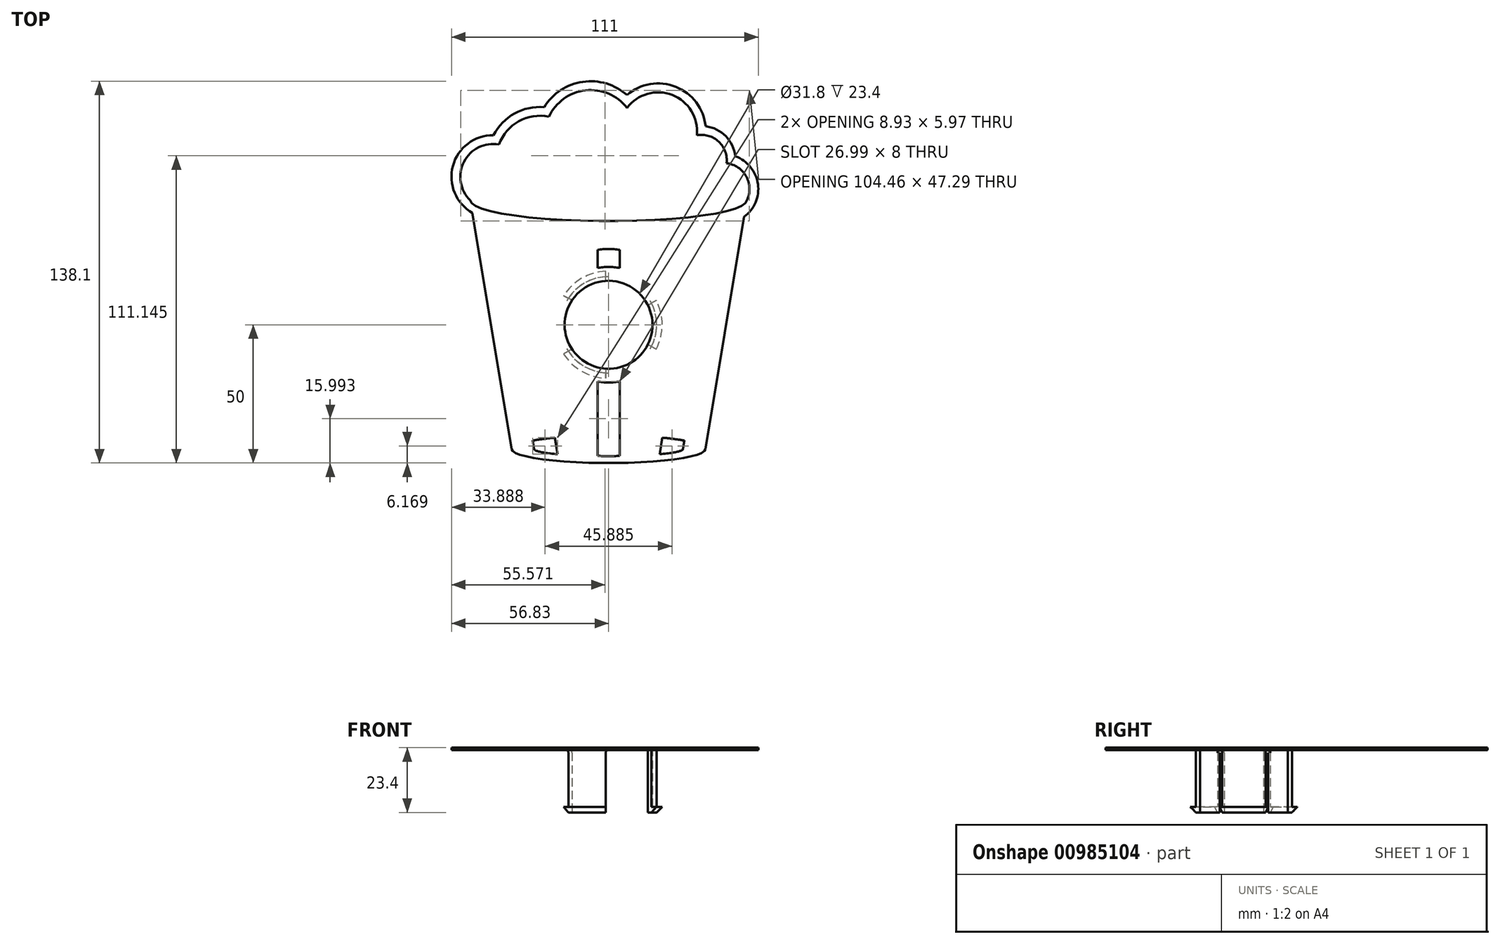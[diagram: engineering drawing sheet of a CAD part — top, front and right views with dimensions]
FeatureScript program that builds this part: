
annotation { "Feature Type Name" : "Feature", "Feature Type Description" : "" }
export const myFeature = defineFeature(function(context is Context, id is Id, definition is map)
    precondition{}
    {
        {
            var Q0;
            Q0=qCreatedBy(makeId("Top.planeOp"),FACE);
            var sketch = newSketch(context, id + "F0", { "sketchPlane" : qUnion([Q0])});
            skCircle(sketch, "E0", {"center": v(0, 0) * mm, "radius": 17.4 * mm});
            skCircle(sketch, "E1", {"center": v(0, 0) * mm, "radius": 15.9 * mm});
            skCircle(sketch, "E2", {"center": v(0, 0) * mm, "radius": 27.4 * mm});
            skLineSegment(sketch, "E3", {"start": v(0, 0) * mm, "end": v(0, 17.75) * mm, "construction": true});
            skText(sketch, "E4", { "text": "o", "fontName": "RobotoSlab-Bold.ttf"});
            skText(sketch, "E5", { "text": "u", "fontName": "RobotoSlab-Bold.ttf"});
            skText(sketch, "E6", { "text": "e", "fontName": "RobotoSlab-Bold.ttf"});
            skText(sketch, "E7", { "text": "i", "fontName": "RobotoSlab-Bold.ttf"});
            skText(sketch, "E8", { "text": "r", "fontName": "RobotoSlab-Bold.ttf"});
            skText(sketch, "E9", { "text": "c", "fontName": "RobotoSlab-Bold.ttf"});
            skText(sketch, "E10", { "text": "e", "fontName": "RobotoSlab-Bold.ttf"});
            skText(sketch, "E11", { "text": "o", "fontName": "RobotoSlab-Bold.ttf"});
            skText(sketch, "E12", { "text": "r", "fontName": "RobotoSlab-Bold.ttf"});
            skText(sketch, "E13", { "text": "n", "fontName": "RobotoSlab-Bold.ttf"});
            skLineSegment(sketch, "E14.2.0", {"start": v(0, 0) * mm, "end": v(-15.37, 8.88) * mm, "construction": true});
            skLineSegment(sketch, "E14.3.0", {"start": v(0, 0) * mm, "end": v(-17.75, 0) * mm, "construction": true});
            skLineSegment(sketch, "E14.4.0", {"start": v(0, 0) * mm, "end": v(-15.37, -8.88) * mm, "construction": true});
            skLineSegment(sketch, "E14.5.0", {"start": v(0, 0) * mm, "end": v(-8.88, -15.37) * mm, "construction": true});
            skLineSegment(sketch, "E14.6.0", {"start": v(0, 0) * mm, "end": v(0, -17.75) * mm, "construction": true});
            skLineSegment(sketch, "E14.7.0", {"start": v(0, 0) * mm, "end": v(8.87, -15.37) * mm, "construction": true});
            skLineSegment(sketch, "E14.8.0", {"start": v(0, 0) * mm, "end": v(15.37, -8.88) * mm, "construction": true});
            skLineSegment(sketch, "E14.9.0", {"start": v(0, 0) * mm, "end": v(17.75, 0) * mm, "construction": true});
            skLineSegment(sketch, "E14.10.0", {"start": v(0, 0) * mm, "end": v(15.37, 8.87) * mm, "construction": true});
            skLineSegment(sketch, "E14.11.0", {"start": v(0, 0) * mm, "end": v(8.88, 15.37) * mm, "construction": true});
            skText(sketch, "E15", { "text": "S", "fontName": "RobotoSlab-Bold.ttf"});
            skLineSegment(sketch, "E16", {"start": v(0, 0) * mm, "end": v(-8.88, 15.37) * mm, "construction": true});
            const initialGuessF0  = {"E4": [-0.00328, 0.01775, 1, 0, 0.008], "E5": [0.0057, 0.0172, 0.86603, -0.5, 0.008], "E6": [0.01692, -0.0062, -0.5, -0.86603, 0.008], "E7": [-0.0071, -0.0164, -0.86603, 0.5, 0.008], "E8": [-0.01407, -0.01114, -0.5, 0.86603, 0.008], "E9": [0.01775, 0.0031, 0, -1, 0.008], "E10": [0.01156, -0.01382, -0.86603, -0.5, 0.008], "E11": [-0.01775, -0.00328, 0, 1, 0.008], "E12": [0.01407, 0.01114, 0.5, -0.86603, 0.008], "E13": [-0.01726, 0.0056, 0.5, 0.86603, 0.008], "E15": [-0.01195, 0.0136, 0.86603, 0.5, 0.008]};
            skSetInitialGuess(sketch, initialGuessF0);
            skSolve(sketch);
        }
        {
            var Q0;
            Q0=makeQuery(id+"F0.imprint","IMPRINT",FACE,{"disambiguationData":[TD([[makeQuery(id+"F0.imprint","IMPRINT",EDGE,{"derivedFrom":sQuery(id+"F0.wireOp",EDGE,"E0")}),1.0]])]});
            var Q1;
            Q1=makeQuery(id+"F0.imprint","IMPRINT",FACE,{"disambiguationData":[TD([[makeQuery(id+"F0.imprint","IMPRINT",EDGE,{"derivedFrom":sQuery(id+"F0.wireOp",EDGE,"E4.sketch_text.stroke-0")}),-1.0]])]});
            var Q2;
            Q2=makeQuery(id+"F0.imprint","IMPRINT",FACE,{"disambiguationData":[TD([[makeQuery(id+"F0.imprint","IMPRINT",EDGE,{"derivedFrom":sQuery(id+"F0.wireOp",EDGE,"E7.sketch_text.stroke-0")}),-1.0]])]});
            var Q3;
            Q3=makeQuery(id+"F0.imprint","IMPRINT",FACE,{"disambiguationData":[TD([[makeQuery(id+"F0.imprint","IMPRINT",EDGE,{"derivedFrom":sQuery(id+"F0.wireOp",EDGE,"E11.sketch_text.stroke-10")}),1.0]])]});
            var Q4;
            Q4=makeQuery(id+"F0.imprint","IMPRINT",FACE,{"disambiguationData":[TD([[makeQuery(id+"F0.imprint","IMPRINT",EDGE,{"derivedFrom":sQuery(id+"F0.wireOp",EDGE,"E9.sketch_text.stroke-0")}),-1.0]])]});
            var Q5;
            Q5=makeQuery(id+"F0.imprint","IMPRINT",FACE,{"disambiguationData":[TD([[makeQuery(id+"F0.imprint","IMPRINT",EDGE,{"derivedFrom":sQuery(id+"F0.wireOp",EDGE,"E10.sketch_text.stroke-0")}),-1.0]])]});
            var Q6;
            Q6=makeQuery(id+"F0.imprint","IMPRINT",FACE,{"disambiguationData":[TD([[makeQuery(id+"F0.imprint","IMPRINT",EDGE,{"derivedFrom":sQuery(id+"F0.wireOp",EDGE,"E6.sketch_text.stroke-0")}),-1.0]])]});
            var Q7;
            Q7=makeQuery(id+"F0.imprint","IMPRINT",FACE,{"disambiguationData":[TD([[makeQuery(id+"F0.imprint","IMPRINT",EDGE,{"derivedFrom":sQuery(id+"F0.wireOp",EDGE,"E12.sketch_text.stroke-0")}),-1.0]])]});
            var Q8;
            Q8=makeQuery(id+"F0.imprint","IMPRINT",FACE,{"disambiguationData":[TD([[makeQuery(id+"F0.imprint","IMPRINT",EDGE,{"derivedFrom":sQuery(id+"F0.wireOp",EDGE,"E5.sketch_text.stroke-0")}),-1.0]])]});
            var Q9;
            Q9=makeQuery(id+"F0.imprint","IMPRINT",FACE,{"disambiguationData":[TD([[makeQuery(id+"F0.imprint","IMPRINT",EDGE,{"derivedFrom":sQuery(id+"F0.wireOp",EDGE,"E0")}),-1.0]])]});
            var Q10;
            Q10=makeQuery(id+"F0.imprint","IMPRINT",FACE,{"disambiguationData":[TD([[makeQuery(id+"F0.imprint","IMPRINT",EDGE,{"derivedFrom":sQuery(id+"F0.wireOp",EDGE,"E5.sketch_text.stroke-10")}),1.0]])]});
            var Q11;
            Q11=makeQuery(id+"F0.imprint","IMPRINT",FACE,{"disambiguationData":[TD([[makeQuery(id+"F0.imprint","IMPRINT",EDGE,{"derivedFrom":sQuery(id+"F0.wireOp",EDGE,"E13.sketch_text.stroke-0")}),-1.0]])]});
            var Q12;
            Q12=makeQuery(id+"F0.imprint","IMPRINT",FACE,{"disambiguationData":[TD([[makeQuery(id+"F0.imprint","IMPRINT",EDGE,{"derivedFrom":sQuery(id+"F0.wireOp",EDGE,"E8.sketch_text.stroke-0")}),-1.0]])]});
            var Q13;
            Q13=makeQuery(id+"F0.imprint","IMPRINT",FACE,{"disambiguationData":[TD([[makeQuery(id+"F0.imprint","IMPRINT",EDGE,{"derivedFrom":sQuery(id+"F0.wireOp",EDGE,"E11.sketch_text.stroke-0")}),-1.0]])]});
            var Q14;
            Q14=makeQuery(id+"F0.imprint","IMPRINT",FACE,{"disambiguationData":[TD([[makeQuery(id+"F0.imprint","IMPRINT",EDGE,{"derivedFrom":sQuery(id+"F0.wireOp",EDGE,"E7.sketch_text.stroke-10")}),-1.0]])]});
            var Q15;
            Q15=makeQuery(id+"F0.imprint","IMPRINT",FACE,{"disambiguationData":[TD([[makeQuery(id+"F0.imprint","IMPRINT",EDGE,{"derivedFrom":sQuery(id+"F0.wireOp",EDGE,"E10.sketch_text.stroke-17")}),1.0]])]});
            var Q16;
            Q16=makeQuery(id+"F0.imprint","IMPRINT",FACE,{"disambiguationData":[TD([[makeQuery(id+"F0.imprint","IMPRINT",EDGE,{"derivedFrom":sQuery(id+"F0.wireOp",EDGE,"E15.sketch_text.stroke-0")}),-1.0]])]});
            var Q17;
            Q17=makeQuery(id+"F0.imprint","IMPRINT",FACE,{"disambiguationData":[TD([[makeQuery(id+"F0.imprint","IMPRINT",EDGE,{"derivedFrom":sQuery(id+"F0.wireOp",EDGE,"E4.sketch_text.stroke-10")}),1.0]])]});
            var Q18;
            Q18=makeQuery(id+"F0.imprint","IMPRINT",FACE,{"disambiguationData":[TD([[makeQuery(id+"F0.imprint","IMPRINT",EDGE,{"derivedFrom":sQuery(id+"F0.wireOp",EDGE,"E6.sketch_text.stroke-17")}),1.0]])]});
            extrude(context, id + "F1", {"entities" : qUnion([Q0, Q1, Q2, Q3, Q4, Q5, Q6, Q7, Q8, Q9, Q10, Q11, Q12, Q13, Q14, Q15, Q16, Q17, Q18]), "depth" : 0.8 * mm, "offsetDistance" : 25 * mm});
        }
        {
            var Q0;
            Q0=makeQuery(id+"F0.imprint","IMPRINT",FACE,{"disambiguationData":[TD([[makeQuery(id+"F0.imprint","IMPRINT",EDGE,{"derivedFrom":sQuery(id+"F0.wireOp",EDGE,"E0")}),1.0]])]});
            extrude(context, id + "F2", {"entities" : qUnion([Q0]), "operationType" : NewBodyOperationType.ADD, "oppositeDirection" : true, "depth" : 22.6 * mm, "offsetDistance" : 25 * mm});
        }
        {
            var Q0;
            Q0=makeQuery(id+"F2.opExtrude","CAP_FACE",FACE,{"disambiguationData":[OSD([sQuery(id+"F0.wireOp",EDGE,"E0"),sQuery(id+"F0.wireOp",EDGE,"E1")])],"isStart":false});
            var sketch = newSketch(context, id + "F3", { "sketchPlane" : qUnion([Q0])});
            skLineSegment(sketch, "E17.bottom", {"start": v(1, 0) * mm, "end": v(-1, 0) * mm});
            skLineSegment(sketch, "E17.top", {"start": v(1, -20) * mm, "end": v(-1, -20) * mm});
            skLineSegment(sketch, "E17.left", {"start": v(1, 0) * mm, "end": v(1, -20) * mm});
            skLineSegment(sketch, "E17.right", {"start": v(-1, 0) * mm, "end": v(-1, -20) * mm});
            skLineSegment(sketch, "E18.1.0", {"start": v(0.5, 0.87) * mm, "end": v(-0.5, -0.87) * mm});
            skLineSegment(sketch, "E18.1.1", {"start": v(17.82, -9.13) * mm, "end": v(16.82, -10.87) * mm});
            skLineSegment(sketch, "E18.1.2", {"start": v(-0.5, -0.87) * mm, "end": v(16.82, -10.87) * mm});
            skLineSegment(sketch, "E18.1.3", {"start": v(0.5, 0.87) * mm, "end": v(17.82, -9.13) * mm});
            skLineSegment(sketch, "E18.2.0", {"start": v(-0.5, 0.87) * mm, "end": v(0.5, -0.87) * mm});
            skLineSegment(sketch, "E18.2.1", {"start": v(16.82, 10.87) * mm, "end": v(17.82, 9.13) * mm});
            skLineSegment(sketch, "E18.2.2", {"start": v(0.5, -0.87) * mm, "end": v(17.82, 9.13) * mm});
            skLineSegment(sketch, "E18.2.3", {"start": v(-0.5, 0.87) * mm, "end": v(16.82, 10.87) * mm});
            skLineSegment(sketch, "E18.3.0", {"start": v(-1, 0) * mm, "end": v(1, 0) * mm});
            skLineSegment(sketch, "E18.3.1", {"start": v(-1, 20) * mm, "end": v(1, 20) * mm});
            skLineSegment(sketch, "E18.3.2", {"start": v(1, 0) * mm, "end": v(1, 20) * mm});
            skLineSegment(sketch, "E18.3.3", {"start": v(-1, 0) * mm, "end": v(-1, 20) * mm});
            skLineSegment(sketch, "E18.4.0", {"start": v(-0.5, -0.87) * mm, "end": v(0.5, 0.87) * mm});
            skLineSegment(sketch, "E18.4.1", {"start": v(-17.82, 9.13) * mm, "end": v(-16.82, 10.87) * mm});
            skLineSegment(sketch, "E18.4.2", {"start": v(0.5, 0.87) * mm, "end": v(-16.82, 10.87) * mm});
            skLineSegment(sketch, "E18.4.3", {"start": v(-0.5, -0.87) * mm, "end": v(-17.82, 9.13) * mm});
            skLineSegment(sketch, "E18.5.0", {"start": v(0.5, -0.87) * mm, "end": v(-0.5, 0.87) * mm});
            skLineSegment(sketch, "E18.5.1", {"start": v(-16.82, -10.87) * mm, "end": v(-17.82, -9.13) * mm});
            skLineSegment(sketch, "E18.5.2", {"start": v(-0.5, 0.87) * mm, "end": v(-17.82, -9.13) * mm});
            skLineSegment(sketch, "E18.5.3", {"start": v(0.5, -0.87) * mm, "end": v(-16.82, -10.87) * mm});
            skPoint(sketch, "E18.center", {"position": v(0, 0) * mm});
            skCircle(sketch, "E19", {"center": v(0, 0) * mm, "radius": 19.4 * mm});
            skSolve(sketch);
        }
        {
            var Q0;
            {var subQ0=sQuery(id+"F3.wireOp",EDGE,"E18.1.2");var subQ1=makeQuery(id+"F2.opExtrude","CAP_EDGE",EDGE,{"disambiguationData":[OSD([sQuery(id+"F0.wireOp",EDGE,"E1")])],"isStart":false});var subQ2=makeQuery(id+"F3.imprint","INTERSECT",VERTEX,{"derivedFrom":[subQ1,subQ0]});Q0=makeQuery(id+"F3.imprint","IMPRINT",FACE,{"disambiguationData":[TD([[makeQuery(id+"F3.imprint","IMPRINT",EDGE,{"disambiguationData":[TD([[subQ2,-1.0]])],"derivedFrom":subQ0}),1.0]])]});}
            var Q1;
            {var subQ0=sQuery(id+"F3.wireOp",EDGE,"E17.left");var subQ1=makeQuery(id+"F2.opExtrude","CAP_EDGE",EDGE,{"disambiguationData":[OSD([sQuery(id+"F0.wireOp",EDGE,"E1")])],"isStart":false});var subQ2=makeQuery(id+"F3.imprint","INTERSECT",VERTEX,{"derivedFrom":[subQ1,subQ0]});Q1=makeQuery(id+"F3.imprint","IMPRINT",FACE,{"disambiguationData":[TD([[makeQuery(id+"F3.imprint","IMPRINT",EDGE,{"disambiguationData":[TD([[subQ2,-1.0]])],"derivedFrom":subQ0}),-1.0]])]});}
            var Q2;
            {var subQ0=sQuery(id+"F3.wireOp",EDGE,"E18.5.2");var subQ1=makeQuery(id+"F2.opExtrude","CAP_EDGE",EDGE,{"disambiguationData":[OSD([sQuery(id+"F0.wireOp",EDGE,"E1")])],"isStart":false});var subQ2=makeQuery(id+"F3.imprint","INTERSECT",VERTEX,{"derivedFrom":[subQ1,subQ0]});Q2=makeQuery(id+"F3.imprint","IMPRINT",FACE,{"disambiguationData":[TD([[makeQuery(id+"F3.imprint","IMPRINT",EDGE,{"disambiguationData":[TD([[subQ2,-1.0]])],"derivedFrom":subQ0}),1.0]])]});}
            var Q3;
            {var subQ0=sQuery(id+"F3.wireOp",EDGE,"E18.4.2");var subQ1=makeQuery(id+"F2.opExtrude","CAP_EDGE",EDGE,{"disambiguationData":[OSD([sQuery(id+"F0.wireOp",EDGE,"E1")])],"isStart":false});var subQ2=makeQuery(id+"F3.imprint","INTERSECT",VERTEX,{"derivedFrom":[subQ1,subQ0]});Q3=makeQuery(id+"F3.imprint","IMPRINT",FACE,{"disambiguationData":[TD([[makeQuery(id+"F3.imprint","IMPRINT",EDGE,{"disambiguationData":[TD([[subQ2,-1.0]])],"derivedFrom":subQ0}),1.0]])]});}
            var Q4;
            {var subQ0=sQuery(id+"F3.wireOp",EDGE,"E18.3.2");var subQ1=makeQuery(id+"F2.opExtrude","CAP_EDGE",EDGE,{"disambiguationData":[OSD([sQuery(id+"F0.wireOp",EDGE,"E1")])],"isStart":false});var subQ2=makeQuery(id+"F3.imprint","INTERSECT",VERTEX,{"derivedFrom":[subQ1,subQ0]});Q4=makeQuery(id+"F3.imprint","IMPRINT",FACE,{"disambiguationData":[TD([[makeQuery(id+"F3.imprint","IMPRINT",EDGE,{"disambiguationData":[TD([[subQ2,-1.0]])],"derivedFrom":subQ0}),1.0]])]});}
            var Q5;
            {var subQ0=sQuery(id+"F3.wireOp",EDGE,"E18.2.2");var subQ1=makeQuery(id+"F2.opExtrude","CAP_EDGE",EDGE,{"disambiguationData":[OSD([sQuery(id+"F0.wireOp",EDGE,"E1")])],"isStart":false});var subQ2=makeQuery(id+"F3.imprint","INTERSECT",VERTEX,{"derivedFrom":[subQ1,subQ0]});Q5=makeQuery(id+"F3.imprint","IMPRINT",FACE,{"disambiguationData":[TD([[makeQuery(id+"F3.imprint","IMPRINT",EDGE,{"disambiguationData":[TD([[subQ2,-1.0]])],"derivedFrom":subQ0}),1.0]])]});}
            var Q6;
            {var subQ0=sQuery(id+"F3.wireOp",EDGE,"E17.left");var subQ1=makeQuery(id+"F2.opExtrude","CAP_EDGE",EDGE,{"disambiguationData":[OSD([sQuery(id+"F0.wireOp",EDGE,"E1")])],"isStart":false});var subQ2=makeQuery(id+"F3.imprint","INTERSECT",VERTEX,{"derivedFrom":[subQ1,subQ0]});Q6=makeQuery(id+"F3.imprint","IMPRINT",FACE,{"disambiguationData":[TD([[makeQuery(id+"F3.imprint","IMPRINT",EDGE,{"disambiguationData":[TD([[subQ2,-1.0]])],"derivedFrom":subQ0}),1.0]])]});}
            var Q7;
            {var subQ0=sQuery(id+"F3.wireOp",EDGE,"E18.4.3");var subQ1=makeQuery(id+"F2.opExtrude","CAP_EDGE",EDGE,{"disambiguationData":[OSD([sQuery(id+"F0.wireOp",EDGE,"E1")])],"isStart":false});var subQ2=makeQuery(id+"F3.imprint","INTERSECT",VERTEX,{"derivedFrom":[subQ1,subQ0]});Q7=makeQuery(id+"F3.imprint","IMPRINT",FACE,{"disambiguationData":[TD([[makeQuery(id+"F3.imprint","IMPRINT",EDGE,{"disambiguationData":[TD([[subQ2,-1.0]])],"derivedFrom":subQ0}),1.0]])]});}
            var Q8;
            {var subQ0=sQuery(id+"F3.wireOp",EDGE,"E18.2.3");var subQ1=makeQuery(id+"F2.opExtrude","CAP_EDGE",EDGE,{"disambiguationData":[OSD([sQuery(id+"F0.wireOp",EDGE,"E1")])],"isStart":false});var subQ2=makeQuery(id+"F3.imprint","INTERSECT",VERTEX,{"derivedFrom":[subQ1,subQ0]});Q8=makeQuery(id+"F3.imprint","IMPRINT",FACE,{"disambiguationData":[TD([[makeQuery(id+"F3.imprint","IMPRINT",EDGE,{"disambiguationData":[TD([[subQ2,-1.0]])],"derivedFrom":subQ0}),1.0]])]});}
            var Q9;
            Q9=makeQuery(id+"F1.opExtrude","CAP_FACE",FACE,{"disambiguationData":[OSD([sQuery(id+"F0.wireOp",EDGE,"E1"),sQuery(id+"F0.wireOp",EDGE,"E2")])],"isStart":true});
            extrude(context, id + "F4", {"entities" : qUnion([Q0, Q1, Q2, Q3, Q4, Q5, Q6, Q7, Q8]), "operationType" : NewBodyOperationType.REMOVE, "endBound" : BoundingType.UP_TO_SURFACE, "oppositeDirection" : true, "depth" : 25 * mm, "endBoundEntityFace" : qUnion([Q9]), "offsetDistance" : 25 * mm});
        }
        {
            var Q0;
            {var subQ0=sQuery(id+"F3.wireOp",EDGE,"E19");var subQ1=sQuery(id+"F3.wireOp",EDGE,"E18.1.3");var subQ2=makeQuery(id+"F3.imprint","INTERSECT",VERTEX,{"derivedFrom":[subQ1,subQ0]});Q0=makeQuery(id+"F3.imprint","IMPRINT",FACE,{"disambiguationData":[TD([[makeQuery(id+"F3.imprint","IMPRINT",EDGE,{"disambiguationData":[TD([[subQ2,1.0]])],"derivedFrom":subQ1}),1.0]])]});}
            var Q1;
            {var subQ0=sQuery(id+"F3.wireOp",EDGE,"E19");var subQ1=sQuery(id+"F3.wireOp",EDGE,"E17.right");var subQ2=makeQuery(id+"F3.imprint","INTERSECT",VERTEX,{"derivedFrom":[subQ1,subQ0]});Q1=makeQuery(id+"F3.imprint","IMPRINT",FACE,{"disambiguationData":[TD([[makeQuery(id+"F3.imprint","IMPRINT",EDGE,{"disambiguationData":[TD([[subQ2,1.0]])],"derivedFrom":subQ1}),-1.0]])]});}
            var Q2;
            {var subQ0=sQuery(id+"F3.wireOp",EDGE,"E19");var subQ1=sQuery(id+"F3.wireOp",EDGE,"E18.3.3");var subQ2=makeQuery(id+"F3.imprint","INTERSECT",VERTEX,{"derivedFrom":[subQ1,subQ0]});Q2=makeQuery(id+"F3.imprint","IMPRINT",FACE,{"disambiguationData":[TD([[makeQuery(id+"F3.imprint","IMPRINT",EDGE,{"disambiguationData":[TD([[subQ2,1.0]])],"derivedFrom":subQ1}),1.0]])]});}
            extrude(context, id + "F5", {"entities" : qUnion([Q0, Q1, Q2]), "operationType" : NewBodyOperationType.ADD, "oppositeDirection" : true, "depth" : 2 * mm, "offsetDistance" : 25 * mm});
        }
        {
            var Q0;
            {var subQ0=sQuery(id+"F3.wireOp",EDGE,"E19");Q0=makeQuery(id+"F5.opExtrude","CAP_EDGE",EDGE,{"disambiguationData":[OSD([subQ0]),TDD([makeQuery(id+"F3.imprint","IMPRINT",EDGE,{"disambiguationData":[TD([[makeQuery(id+"F3.imprint","INTERSECT",VERTEX,{"derivedFrom":[sQuery(id+"F3.wireOp",EDGE,"E18.1.3"),subQ0]}),-1.0]])],"derivedFrom":subQ0})])],"isStart":true});}
            var Q1;
            {var subQ0=sQuery(id+"F3.wireOp",EDGE,"E19");Q1=makeQuery(id+"F5.opExtrude","CAP_EDGE",EDGE,{"disambiguationData":[OSD([subQ0]),TDD([makeQuery(id+"F3.imprint","IMPRINT",EDGE,{"disambiguationData":[TD([[makeQuery(id+"F3.imprint","INTERSECT",VERTEX,{"derivedFrom":[sQuery(id+"F3.wireOp",EDGE,"E18.2.3"),subQ0]}),-1.0]])],"derivedFrom":subQ0})])],"isStart":true});}
            var Q2;
            {var subQ0=sQuery(id+"F3.wireOp",EDGE,"E19");Q2=makeQuery(id+"F5.opExtrude","CAP_EDGE",EDGE,{"disambiguationData":[OSD([subQ0]),TDD([makeQuery(id+"F3.imprint","IMPRINT",EDGE,{"disambiguationData":[TD([[makeQuery(id+"F3.imprint","INTERSECT",VERTEX,{"derivedFrom":[sQuery(id+"F3.wireOp",EDGE,"E18.3.3"),subQ0]}),-1.0]])],"derivedFrom":subQ0})])],"isStart":true});}
            var Q3;
            {var subQ0=sQuery(id+"F3.wireOp",EDGE,"E19");Q3=makeQuery(id+"F5.opExtrude","CAP_EDGE",EDGE,{"disambiguationData":[OSD([subQ0]),TDD([makeQuery(id+"F3.imprint","IMPRINT",EDGE,{"disambiguationData":[TD([[makeQuery(id+"F3.imprint","INTERSECT",VERTEX,{"derivedFrom":[sQuery(id+"F3.wireOp",EDGE,"E17.right"),subQ0]}),1.0]])],"derivedFrom":subQ0})])],"isStart":true});}
            var Q4;
            {var subQ0=sQuery(id+"F3.wireOp",EDGE,"E19");Q4=makeQuery(id+"F5.opExtrude","CAP_EDGE",EDGE,{"disambiguationData":[OSD([subQ0]),TDD([makeQuery(id+"F3.imprint","IMPRINT",EDGE,{"disambiguationData":[TD([[makeQuery(id+"F3.imprint","INTERSECT",VERTEX,{"derivedFrom":[sQuery(id+"F3.wireOp",EDGE,"E17.left"),subQ0]}),-1.0]])],"derivedFrom":subQ0})])],"isStart":true});}
            var Q5;
            {var subQ0=sQuery(id+"F3.wireOp",EDGE,"E19");Q5=makeQuery(id+"F5.opExtrude","CAP_EDGE",EDGE,{"disambiguationData":[OSD([subQ0]),TDD([makeQuery(id+"F3.imprint","IMPRINT",EDGE,{"disambiguationData":[TD([[makeQuery(id+"F3.imprint","INTERSECT",VERTEX,{"derivedFrom":[sQuery(id+"F3.wireOp",EDGE,"E18.4.3"),subQ0]}),-1.0]])],"derivedFrom":subQ0})])],"isStart":true});}
            chamfer(context, id + "F6", {"entities" : qUnion([Q0, Q1, Q2, Q3, Q4, Q5]), "width" : 2 * mm, "tangentPropagation" : true});
        }
        {
            var Q0;
            {var subQ0=sQuery(id+"F3.wireOp",EDGE,"E17.right");var subQ2=sQuery(id+"F0.wireOp",EDGE,"E0");Q0=makeQuery(id+"F4.boolean.opBoolean","SPLIT",EDGE,{"disambiguationData":[TD([makeQuery(id+"F4.opExtrude","SWEPT_FACE",FACE,{"disambiguationData":[OSD([subQ0])]})])],"derivedFrom":makeQuery(id+"F2.opExtrude","CAP_EDGE",EDGE,{"disambiguationData":[OSD([subQ2])],"isStart":true})});}
            var Q1;
            {var subQ1=sQuery(id+"F0.wireOp",EDGE,"E0");var subQ2=sQuery(id+"F3.wireOp",EDGE,"E18.3.3");Q1=makeQuery(id+"F4.boolean.opBoolean","SPLIT",EDGE,{"disambiguationData":[TD([makeQuery(id+"F4.opExtrude","SWEPT_FACE",FACE,{"disambiguationData":[OSD([subQ2])]})])],"derivedFrom":makeQuery(id+"F2.opExtrude","CAP_EDGE",EDGE,{"disambiguationData":[OSD([subQ1])],"isStart":true})});}
            var Q2;
            {var subQ0=sQuery(id+"F3.wireOp",EDGE,"E18.1.3");var subQ2=sQuery(id+"F0.wireOp",EDGE,"E0");Q2=makeQuery(id+"F4.boolean.opBoolean","SPLIT",EDGE,{"disambiguationData":[TD([makeQuery(id+"F4.opExtrude","SWEPT_FACE",FACE,{"disambiguationData":[OSD([subQ0])]})])],"derivedFrom":makeQuery(id+"F2.opExtrude","CAP_EDGE",EDGE,{"disambiguationData":[OSD([subQ2])],"isStart":true})});}
            var Q3;
            Q3=makeQuery(id+"F4.boolean.opBoolean","COPY",EDGE,{"derivedFrom":makeQuery(id+"F4.opExtrude","CAP_EDGE",EDGE,{"disambiguationData":[OSD([sQuery(id+"F3.wireOp",EDGE,"E18.2.2")])],"isStart":false})});
            var Q4;
            Q4=makeQuery(id+"F4.boolean.opBoolean","COPY",EDGE,{"derivedFrom":makeQuery(id+"F4.opExtrude","CAP_EDGE",EDGE,{"disambiguationData":[OSD([sQuery(id+"F3.wireOp",EDGE,"E18.3.3")])],"isStart":false})});
            var Q5;
            Q5=makeQuery(id+"F4.boolean.opBoolean","COPY",EDGE,{"derivedFrom":makeQuery(id+"F4.opExtrude","CAP_EDGE",EDGE,{"disambiguationData":[OSD([sQuery(id+"F3.wireOp",EDGE,"E18.1.3")])],"isStart":false})});
            var Q6;
            Q6=makeQuery(id+"F4.boolean.opBoolean","COPY",EDGE,{"derivedFrom":makeQuery(id+"F4.opExtrude","CAP_EDGE",EDGE,{"disambiguationData":[OSD([sQuery(id+"F3.wireOp",EDGE,"E17.right")])],"isStart":false})});
            var Q7;
            Q7=makeQuery(id+"F4.boolean.opBoolean","COPY",EDGE,{"derivedFrom":makeQuery(id+"F4.opExtrude","CAP_EDGE",EDGE,{"disambiguationData":[OSD([sQuery(id+"F3.wireOp",EDGE,"E18.5.3")])],"isStart":false})});
            var Q8;
            Q8=makeQuery(id+"F4.boolean.opBoolean","COPY",EDGE,{"derivedFrom":makeQuery(id+"F4.opExtrude","CAP_EDGE",EDGE,{"disambiguationData":[OSD([sQuery(id+"F3.wireOp",EDGE,"E18.4.2")])],"isStart":false})});
            fillet(context, id + "F7", {"entities" : qUnion([Q0, Q1, Q2, Q3, Q4, Q5, Q6, Q7, Q8]), "radius" : 1 * mm, "tangentPropagation" : true, "allowEdgeOverflow" : false});
        }
        {
            var Q0;
            Q0=makeQuery(id+"F1.opExtrude","CAP_FACE",FACE,{"disambiguationData":[OSD([sQuery(id+"F0.wireOp",EDGE,"E1"),sQuery(id+"F0.wireOp",EDGE,"E2")])],"isStart":false});
            var sketch = newSketch(context, id + "F8", { "sketchPlane" : qUnion([Q0])});
            skLineSegment(sketch, "E20", {"start": v(0, -45) * mm, "end": v(0, 45) * mm, "construction": true});
            skEllipse(sketch, "E21", {"center": v(0, -45) * mm, "majorRadius": 35 * mm, "minorRadius": 5 * mm, "majorAxis": v(-1, 0)});
            skEllipticalArc(sketch, "E22", {});
            skLineSegment(sketch, "E23", {"start": v(-35, -45) * mm, "end": v(-49.94, 44.63) * mm});
            skLineSegment(sketch, "E24", {"start": v(35, -45) * mm, "end": v(49.94, 44.63) * mm});
            skLineSegment(sketch, "E25.0", {"start": v(-26.89, -45) * mm, "end": v(-40.3, 35.46) * mm});
            skLineSegment(sketch, "E26.0", {"start": v(-18.48, -46.82) * mm, "end": v(-31.98, 34.2) * mm});
            skEllipse(sketch, "E27", {"center": v(0, -45) * mm, "majorRadius": 26.89 * mm, "minorRadius": 2.5 * mm, "majorAxis": v(-1, 0)});
            skPoint(sketch, "E28", {"position": v(-26.89, -45) * mm});
            skLineSegment(sketch, "E29", {"start": v(-4, 32.52) * mm, "end": v(-4, -47.47) * mm});
            skFitSpline(sketch, "E30.0", {"points": [v(54.94, 43.99) * mm, v(55.03, 45) * mm, v(54.94, 46.01) * mm, v(54.7, 46.96) * mm, v(54.35, 47.8) * mm, v(53.79, 48.76) * mm, v(53, 49.68) * mm, v(52.03, 50.5) * mm, v(51.06, 51.14) * mm, v(50.06, 51.68) * mm, v(49.01, 52.15) * mm, v(47.54, 52.72) * mm, v(45.52, 53.36) * mm, v(42.76, 54.05) * mm, v(40.16, 54.58) * mm, v(37.9, 54.97) * mm, v(36.11, 55.25) * mm, v(34.24, 55.52) * mm, v(31.66, 55.85) * mm, v(28.28, 56.23) * mm, v(23.98, 56.61) * mm, v(19.47, 56.93) * mm, v(14.8, 57.18) * mm, v(9.97, 57.36) * mm, v(5.85, 57.46) * mm, v(2.52, 57.5) * mm, v(0, 57.5) * mm, v(-2.52, 57.5) * mm, v(-5.85, 57.46) * mm, v(-9.97, 57.36) * mm, v(-14.8, 57.18) * mm, v(-19.47, 56.93) * mm, v(-23.98, 56.61) * mm, v(-28.28, 56.23) * mm, v(-31.66, 55.85) * mm, v(-34.24, 55.52) * mm, v(-36.11, 55.25) * mm, v(-37.9, 54.97) * mm, v(-40.16, 54.58) * mm, v(-42.76, 54.05) * mm, v(-45.52, 53.36) * mm, v(-47.54, 52.72) * mm, v(-49.01, 52.15) * mm, v(-50.06, 51.68) * mm, v(-51.06, 51.14) * mm, v(-52.03, 50.5) * mm, v(-53, 49.68) * mm, v(-53.79, 48.76) * mm, v(-54.35, 47.8) * mm, v(-54.7, 46.96) * mm, v(-54.94, 46.01) * mm, v(-55.03, 45) * mm, v(-54.94, 43.99) * mm, v(-54.7, 43.04) * mm, v(-54.35, 42.2) * mm, v(-53.79, 41.24) * mm, v(-53, 40.32) * mm, v(-52.03, 39.5) * mm, v(-51.06, 38.86) * mm, v(-50.06, 38.32) * mm, v(-49.01, 37.85) * mm, v(-47.54, 37.28) * mm, v(-45.52, 36.64) * mm, v(-42.76, 35.95) * mm, v(-40.16, 35.42) * mm, v(-37.9, 35.03) * mm, v(-36.11, 34.75) * mm, v(-34.24, 34.48) * mm, v(-31.66, 34.15) * mm, v(-28.28, 33.77) * mm, v(-23.98, 33.39) * mm, v(-19.47, 33.07) * mm, v(-14.8, 32.82) * mm, v(-9.97, 32.64) * mm, v(-5.85, 32.54) * mm, v(-2.52, 32.5) * mm, v(0, 32.5) * mm, v(2.52, 32.5) * mm, v(5.85, 32.54) * mm, v(9.97, 32.64) * mm, v(14.8, 32.82) * mm, v(19.47, 33.07) * mm, v(23.98, 33.39) * mm, v(28.28, 33.77) * mm, v(31.66, 34.15) * mm, v(34.24, 34.48) * mm, v(36.11, 34.75) * mm, v(37.9, 35.03) * mm, v(40.16, 35.42) * mm, v(42.76, 35.95) * mm, v(45.52, 36.64) * mm, v(47.54, 37.28) * mm, v(49.01, 37.85) * mm, v(50.06, 38.32) * mm, v(51.06, 38.86) * mm, v(52.03, 39.5) * mm, v(53, 40.32) * mm, v(53.79, 41.24) * mm, v(54.35, 42.2) * mm, v(54.7, 43.04) * mm, v(54.94, 43.99) * mm, v(55.03, 45) * mm, v(54.94, 46.01) * mm]});
            skLineSegment(sketch, "E31.MirrorCS", {"start": v(4, 32.52) * mm, "end": v(4, -47.47) * mm});
            skLineSegment(sketch, "E32.MirrorCS", {"start": v(18.48, -46.82) * mm, "end": v(31.98, 34.2) * mm});
            skLineSegment(sketch, "E33.MirrorCS", {"start": v(26.89, -45) * mm, "end": v(40.3, 35.46) * mm});
            skCircle(sketch, "E34.0", {"center": v(0, 0) * mm, "radius": 20.9 * mm});
            skArc(sketch, "E35.trimOffspring", {"start": v(-39.63, 65.17) * mm, "mid": v(-52.32, 58.94) * mm, "end": v(-50, 45) * mm});
            skArc(sketch, "E36.trimOffspring", {"start": v(-21.56, 75.23) * mm, "mid": v(-32.5, 73.61) * mm, "end": v(-39.63, 65.17) * mm});
            skArc(sketch, "E37.trimOffspring", {"start": v(6.67, 78.45) * mm, "mid": v(-8.35, 84.79) * mm, "end": v(-21.56, 75.23) * mm});
            skArc(sketch, "E38.trimOffspring", {"start": v(31.95, 68.57) * mm, "mid": v(23.07, 83.1) * mm, "end": v(6.67, 78.45) * mm});
            skArc(sketch, "E39.trimOffspring", {"start": v(50, 45) * mm, "mid": v(49.84, 53.6) * mm, "end": v(42.7, 58.4) * mm});
            skArc(sketch, "E40.trimOffspring", {"start": v(42.7, 58.4) * mm, "mid": v(39.88, 66.2) * mm, "end": v(31.95, 68.57) * mm});
            skArc(sketch, "E41.0", {"start": v(-23.3, 78.72) * mm, "mid": v(-34.01, 76.43) * mm, "end": v(-41.64, 68.57) * mm});
            skArc(sketch, "E41.1", {"start": v(6.68, 83.1) * mm, "mid": v(-9.33, 87.89) * mm, "end": v(-23.3, 78.72) * mm});
            skArc(sketch, "E41.3", {"start": v(29.21, 47.87) * mm, "mid": v(49.38, 39.3) * mm, "end": v(45.88, 60.93) * mm});
            skArc(sketch, "E41.4", {"start": v(45.88, 60.93) * mm, "mid": v(42.38, 68.22) * mm, "end": v(35.12, 71.8) * mm});
            skArc(sketch, "E41.5", {"start": v(-41.64, 68.57) * mm, "mid": v(-55.85, 48.17) * mm, "end": v(-31.67, 42.42) * mm});
            skArc(sketch, "E41.6", {"start": v(35.12, 71.8) * mm, "mid": v(24.32, 86.05) * mm, "end": v(6.68, 83.1) * mm});
            skFitSpline(sketch, "E42.0", {"points": [v(53.26, 44.27) * mm, v(53.33, 45) * mm, v(53.26, 45.73) * mm, v(53.1, 46.42) * mm, v(52.83, 47.04) * mm, v(52.41, 47.76) * mm, v(51.8, 48.47) * mm, v(51.02, 49.13) * mm, v(50.2, 49.68) * mm, v(49.02, 50.31) * mm, v(47.38, 51) * mm, v(45.06, 51.72) * mm, v(42.39, 52.4) * mm, v(39.84, 52.9) * mm, v(37.62, 53.3) * mm, v(35.86, 53.57) * mm, v(34.01, 53.84) * mm, v(31.46, 54.17) * mm, v(28.1, 54.54) * mm, v(23.84, 54.92) * mm, v(19.37, 55.24) * mm, v(14.72, 55.49) * mm, v(9.92, 55.67) * mm, v(5.82, 55.76) * mm, v(2.5, 55.8) * mm, v(0, 55.8) * mm, v(-2.5, 55.8) * mm, v(-5.82, 55.76) * mm, v(-9.92, 55.67) * mm, v(-14.72, 55.49) * mm, v(-19.37, 55.24) * mm, v(-23.84, 54.92) * mm, v(-28.1, 54.54) * mm, v(-31.46, 54.17) * mm, v(-34.01, 53.84) * mm, v(-35.86, 53.57) * mm, v(-37.62, 53.3) * mm, v(-39.84, 52.9) * mm, v(-42.39, 52.4) * mm, v(-45.06, 51.72) * mm, v(-47.38, 51) * mm, v(-49.02, 50.31) * mm, v(-50.2, 49.68) * mm, v(-51.02, 49.13) * mm, v(-51.8, 48.47) * mm, v(-52.41, 47.76) * mm, v(-52.83, 47.04) * mm, v(-53.1, 46.42) * mm, v(-53.26, 45.73) * mm, v(-53.33, 45) * mm, v(-53.26, 44.27) * mm, v(-53.1, 43.58) * mm, v(-52.83, 42.96) * mm, v(-52.41, 42.24) * mm, v(-51.8, 41.53) * mm, v(-51.02, 40.87) * mm, v(-50.2, 40.32) * mm, v(-49.02, 39.69) * mm, v(-47.38, 39) * mm, v(-45.06, 38.28) * mm, v(-42.39, 37.6) * mm, v(-39.84, 37.1) * mm, v(-37.62, 36.7) * mm, v(-35.86, 36.43) * mm, v(-34.01, 36.16) * mm, v(-31.46, 35.83) * mm, v(-28.1, 35.46) * mm, v(-23.84, 35.08) * mm, v(-19.37, 34.76) * mm, v(-14.72, 34.51) * mm, v(-9.92, 34.33) * mm, v(-5.82, 34.24) * mm, v(-2.5, 34.2) * mm, v(0, 34.2) * mm, v(2.5, 34.2) * mm, v(5.82, 34.24) * mm, v(9.92, 34.33) * mm, v(14.72, 34.51) * mm, v(19.37, 34.76) * mm, v(23.84, 35.08) * mm, v(28.1, 35.46) * mm, v(31.46, 35.83) * mm, v(34.01, 36.16) * mm, v(35.86, 36.43) * mm, v(37.62, 36.7) * mm, v(39.84, 37.1) * mm, v(42.39, 37.6) * mm, v(45.06, 38.28) * mm, v(47.38, 39) * mm, v(49.02, 39.69) * mm, v(50.2, 40.32) * mm, v(51.02, 40.87) * mm, v(51.8, 41.53) * mm, v(52.41, 42.24) * mm, v(52.83, 42.96) * mm, v(53.1, 43.58) * mm, v(53.26, 44.27) * mm, v(53.33, 45) * mm, v(53.26, 45.73) * mm]});
            const initialGuessF8  = {"E22": [0, 0.045, 1, 0, 0.05, 0.0075, 3.141592653589793, 0]};
            skSetInitialGuess(sketch, initialGuessF8);
            skSolve(sketch);
        }
        {
            var Q0;
            {var subQ0=sQuery(id+"F8.wireOp",EDGE,"E23");var subQ1=sQuery(id+"F8.wireOp",EDGE,"E21");var subQ2=makeQuery(id+"F8.imprint","INTERSECT",VERTEX,{"derivedFrom":[subQ1,subQ0]});Q0=makeQuery(id+"F8.imprint","IMPRINT",FACE,{"disambiguationData":[TD([[makeQuery(id+"F8.imprint","IMPRINT",EDGE,{"disambiguationData":[TD([[subQ2,1.0]])],"derivedFrom":subQ1}),-1.0]])]});}
            var Q1;
            {var subQ3=sQuery(id+"F8.wireOp",EDGE,"E21");var subQ8=makeQuery(id+"F8.imprint","INTERSECT",VERTEX,{"derivedFrom":[subQ3,sQuery(id+"F8.wireOp",EDGE,"E23")]});Q1=makeQuery(id+"F8.imprint","IMPRINT",FACE,{"disambiguationData":[TD([[makeQuery(id+"F8.imprint","IMPRINT",EDGE,{"disambiguationData":[TD([[subQ8,-1.0]])],"derivedFrom":subQ3}),1.0]])]});}
            var Q2;
            {var subQ0=sQuery(id+"F8.wireOp",EDGE,"E24");var subQ1=sQuery(id+"F8.wireOp",EDGE,"E21");var subQ2=makeQuery(id+"F8.imprint","INTERSECT",VERTEX,{"derivedFrom":[subQ1,subQ0]});Q2=makeQuery(id+"F8.imprint","IMPRINT",FACE,{"disambiguationData":[TD([[makeQuery(id+"F8.imprint","IMPRINT",EDGE,{"disambiguationData":[TD([[subQ2,-1.0]])],"derivedFrom":subQ1}),-1.0]])]});}
            var Q3;
            {var subQ0=sQuery(id+"F8.wireOp",EDGE,"E32.MirrorCS");var subQ1=sQuery(id+"F8.wireOp",EDGE,"E21");var subQ2=makeQuery(id+"F8.imprint","INTERSECT",VERTEX,{"derivedFrom":[subQ1,subQ0]});Q3=makeQuery(id+"F8.imprint","IMPRINT",FACE,{"disambiguationData":[TD([[makeQuery(id+"F8.imprint","IMPRINT",EDGE,{"disambiguationData":[TD([[subQ2,-1.0]])],"derivedFrom":subQ1}),-1.0]])]});}
            var Q4;
            {var subQ0=sQuery(id+"F8.wireOp",EDGE,"E32.MirrorCS");var subQ1=sQuery(id+"F8.wireOp",EDGE,"E21");var subQ2=makeQuery(id+"F8.imprint","INTERSECT",VERTEX,{"derivedFrom":[subQ1,subQ0]});Q4=makeQuery(id+"F8.imprint","IMPRINT",FACE,{"disambiguationData":[TD([[makeQuery(id+"F8.imprint","IMPRINT",EDGE,{"disambiguationData":[TD([[subQ2,-1.0]])],"derivedFrom":subQ1}),1.0]])]});}
            var Q5;
            {var subQ0=sQuery(id+"F8.wireOp",EDGE,"E31.MirrorCS");var subQ1=sQuery(id+"F8.wireOp",EDGE,"E27");var subQ2=makeQuery(id+"F8.imprint","INTERSECT",VERTEX,{"disambiguationData":[OD(0.0)],"derivedFrom":[subQ1,subQ0]});Q5=makeQuery(id+"F8.imprint","IMPRINT",FACE,{"disambiguationData":[TD([[makeQuery(id+"F8.imprint","IMPRINT",EDGE,{"disambiguationData":[TD([[subQ2,-1.0]])],"derivedFrom":subQ1}),1.0]])]});}
            var Q6;
            {var subQ0=sQuery(id+"F8.wireOp",EDGE,"E27");var subQ1=sQuery(id+"F8.wireOp",EDGE,"E26.0");var subQ2=makeQuery(id+"F8.imprint","INTERSECT",VERTEX,{"disambiguationData":[OD(0.0)],"derivedFrom":[subQ1,subQ0]});Q6=makeQuery(id+"F8.imprint","IMPRINT",FACE,{"disambiguationData":[TD([[makeQuery(id+"F8.imprint","IMPRINT",EDGE,{"disambiguationData":[TD([[subQ2,-1.0]])],"derivedFrom":subQ1}),-1.0]])]});}
            var Q7;
            {var subQ0=sQuery(id+"F8.wireOp",EDGE,"E29");var subQ1=sQuery(id+"F8.wireOp",EDGE,"E21");var subQ2=makeQuery(id+"F8.imprint","INTERSECT",VERTEX,{"derivedFrom":[subQ1,subQ0]});Q7=makeQuery(id+"F8.imprint","IMPRINT",FACE,{"disambiguationData":[TD([[makeQuery(id+"F8.imprint","IMPRINT",EDGE,{"disambiguationData":[TD([[subQ2,-1.0]])],"derivedFrom":subQ1}),-1.0]])]});}
            var Q8;
            {var subQ0=sQuery(id+"F8.wireOp",EDGE,"E30.0");var subQ1=sQuery(id+"F8.wireOp",EDGE,"E26.0");var subQ2=makeQuery(id+"F8.imprint","INTERSECT",VERTEX,{"derivedFrom":[subQ1,subQ0]});Q8=makeQuery(id+"F8.imprint","IMPRINT",FACE,{"disambiguationData":[TD([[makeQuery(id+"F8.imprint","IMPRINT",EDGE,{"disambiguationData":[TD([[subQ2,1.0]])],"derivedFrom":subQ1}),-1.0]])]});}
            var Q9;
            {var subQ0=sQuery(id+"F8.wireOp",EDGE,"E31.MirrorCS");var subQ1=sQuery(id+"F8.wireOp",EDGE,"E30.0");var subQ2=makeQuery(id+"F8.imprint","INTERSECT",VERTEX,{"derivedFrom":[subQ1,subQ0]});Q9=makeQuery(id+"F8.imprint","IMPRINT",FACE,{"disambiguationData":[TD([[makeQuery(id+"F8.imprint","IMPRINT",EDGE,{"disambiguationData":[TD([[subQ2,-1.0]])],"derivedFrom":subQ1}),-1.0]])]});}
            var Q10;
            {var subQ4=sQuery(id+"F8.wireOp",EDGE,"E22");var subQ10=sQuery(id+"F8.wireOp",EDGE,"E23");var subQ11=makeQuery(id+"F8.imprint","INTERSECT",VERTEX,{"derivedFrom":[subQ4,subQ10]});Q10=makeQuery(id+"F8.imprint","IMPRINT",FACE,{"disambiguationData":[TD([[makeQuery(id+"F8.imprint","IMPRINT",EDGE,{"disambiguationData":[TD([[subQ11,-1.0]])],"derivedFrom":subQ4}),-1.0]])]});}
            var Q11;
            {var subQ1=sQuery(id+"F8.wireOp",EDGE,"E22");var subQ3=sQuery(id+"F8.wireOp",EDGE,"xjPRXnkF-zCrR-qSy3-F9DF-8FP80UqlAUpK");var subQ4=makeQuery(id+"F8.imprint","INTERSECT",VERTEX,{"disambiguationData":[OD(1.0)],"derivedFrom":[subQ1,subQ3]});Q11=makeQuery(id+"F8.imprint","IMPRINT",FACE,{"disambiguationData":[TD([[makeQuery(id+"F8.imprint","IMPRINT",EDGE,{"disambiguationData":[TD([[subQ4,-1.0]])],"derivedFrom":subQ3}),-1.0]])]});}
            var Q12;
            {var subQ1=sQuery(id+"F8.wireOp",EDGE,"E22");var subQ3=sQuery(id+"F8.wireOp",EDGE,"xjPRXnkF-zCrR-qSy3-F9DF-8FP80UqlAUpK");var subQ4=makeQuery(id+"F8.imprint","INTERSECT",VERTEX,{"disambiguationData":[OD(1.0)],"derivedFrom":[subQ1,subQ3]});Q12=makeQuery(id+"F8.imprint","IMPRINT",FACE,{"disambiguationData":[TD([[makeQuery(id+"F8.imprint","IMPRINT",EDGE,{"disambiguationData":[TD([[subQ4,1.0]])],"derivedFrom":subQ3}),-1.0]])]});}
            var Q13;
            {var subQ0=sQuery(id+"F8.wireOp",EDGE,"xjPRXnkF-zCrR-qSy3-F9DF-8FP80UqlAUpK");var subQ1=sQuery(id+"F8.wireOp",EDGE,"ZrooK5EC-0a0A-ZKfd-yhxf-CoBbZ34mh2aH");var subQ2=makeQuery(id+"F8.imprint","INTERSECT",VERTEX,{"disambiguationData":[OD(0.0)],"derivedFrom":[subQ1,subQ0]});Q13=makeQuery(id+"F8.imprint","IMPRINT",FACE,{"disambiguationData":[TD([[makeQuery(id+"F8.imprint","IMPRINT",EDGE,{"disambiguationData":[TD([[subQ2,-1.0]])],"derivedFrom":subQ1}),1.0]])]});}
            var Q14;
            {var subQ0=sQuery(id+"F8.wireOp",EDGE,"ZrooK5EC-0a0A-ZKfd-yhxf-CoBbZ34mh2aH");var subQ1=sQuery(id+"F8.wireOp",EDGE,"E22");var subQ2=makeQuery(id+"F8.imprint","INTERSECT",VERTEX,{"derivedFrom":[subQ1,subQ0]});Q14=makeQuery(id+"F8.imprint","IMPRINT",FACE,{"disambiguationData":[TD([[makeQuery(id+"F8.imprint","IMPRINT",EDGE,{"disambiguationData":[TD([[subQ2,-1.0]])],"derivedFrom":subQ1}),-1.0]])]});}
            var Q15;
            {var subQ0=sQuery(id+"F8.wireOp",EDGE,"xjPRXnkF-zCrR-qSy3-F9DF-8FP80UqlAUpK");var subQ1=sQuery(id+"F8.wireOp",EDGE,"ZrooK5EC-0a0A-ZKfd-yhxf-CoBbZ34mh2aH");var subQ2=makeQuery(id+"F8.imprint","INTERSECT",VERTEX,{"disambiguationData":[OD(0.0)],"derivedFrom":[subQ1,subQ0]});Q15=makeQuery(id+"F8.imprint","IMPRINT",FACE,{"disambiguationData":[TD([[makeQuery(id+"F8.imprint","IMPRINT",EDGE,{"disambiguationData":[TD([[subQ2,1.0]])],"derivedFrom":subQ1}),-1.0]])]});}
            var Q16;
            {var subQ0=sQuery(id+"F8.wireOp",EDGE,"CzXEVSpi-58KO-UlYB-svJQ-14zqcH1Ih517");var subQ1=sQuery(id+"F8.wireOp",EDGE,"xjPRXnkF-zCrR-qSy3-F9DF-8FP80UqlAUpK");var subQ2=makeQuery(id+"F8.imprint","INTERSECT",VERTEX,{"disambiguationData":[OD(0.0)],"derivedFrom":[subQ1,subQ0]});Q16=makeQuery(id+"F8.imprint","IMPRINT",FACE,{"disambiguationData":[TD([[makeQuery(id+"F8.imprint","IMPRINT",EDGE,{"disambiguationData":[TD([[subQ2,1.0]])],"derivedFrom":subQ1}),1.0]])]});}
            var Q17;
            {var subQ0=sQuery(id+"F8.wireOp",EDGE,"CzXEVSpi-58KO-UlYB-svJQ-14zqcH1Ih517");var subQ1=sQuery(id+"F8.wireOp",EDGE,"xjPRXnkF-zCrR-qSy3-F9DF-8FP80UqlAUpK");var subQ2=makeQuery(id+"F8.imprint","INTERSECT",VERTEX,{"disambiguationData":[OD(1.0)],"derivedFrom":[subQ1,subQ0]});Q17=makeQuery(id+"F8.imprint","IMPRINT",FACE,{"disambiguationData":[TD([[makeQuery(id+"F8.imprint","IMPRINT",EDGE,{"disambiguationData":[TD([[subQ2,-1.0]])],"derivedFrom":subQ1}),1.0]])]});}
            var Q18;
            {var subQ0=sQuery(id+"F8.wireOp",EDGE,"xjPRXnkF-zCrR-qSy3-F9DF-8FP80UqlAUpK");var subQ1=sQuery(id+"F8.wireOp",EDGE,"ZrooK5EC-0a0A-ZKfd-yhxf-CoBbZ34mh2aH");var subQ2=makeQuery(id+"F8.imprint","INTERSECT",VERTEX,{"disambiguationData":[OD(0.0)],"derivedFrom":[subQ1,subQ0]});Q18=makeQuery(id+"F8.imprint","IMPRINT",FACE,{"disambiguationData":[TD([[makeQuery(id+"F8.imprint","IMPRINT",EDGE,{"disambiguationData":[TD([[subQ2,1.0]])],"derivedFrom":subQ1}),1.0]])]});}
            var Q19;
            {var subQ1=sQuery(id+"F8.wireOp",EDGE,"E22");var subQ6=sQuery(id+"F8.wireOp",EDGE,"xjPRXnkF-zCrR-qSy3-F9DF-8FP80UqlAUpK");var subQ9=makeQuery(id+"F8.imprint","INTERSECT",VERTEX,{"disambiguationData":[OD(0.0)],"derivedFrom":[subQ1,subQ6]});Q19=makeQuery(id+"F8.imprint","IMPRINT",FACE,{"disambiguationData":[TD([[makeQuery(id+"F8.imprint","IMPRINT",EDGE,{"disambiguationData":[TD([[subQ9,-1.0]])],"derivedFrom":subQ1}),-1.0]])]});}
            var Q20;
            {var subQ0=sQuery(id+"F8.wireOp",EDGE,"CzXEVSpi-58KO-UlYB-svJQ-14zqcH1Ih517");var subQ1=sQuery(id+"F8.wireOp",EDGE,"E22");var subQ5=makeQuery(id+"F8.imprint","INTERSECT",VERTEX,{"disambiguationData":[OD(0.0)],"derivedFrom":[subQ1,subQ0]});Q20=makeQuery(id+"F8.imprint","IMPRINT",FACE,{"disambiguationData":[TD([[makeQuery(id+"F8.imprint","IMPRINT",EDGE,{"disambiguationData":[TD([[subQ5,-1.0]])],"derivedFrom":subQ1}),-1.0]])]});}
            var Q21;
            {var subQ1=sQuery(id+"F8.wireOp",EDGE,"CzXEVSpi-58KO-UlYB-svJQ-14zqcH1Ih517");var subQ6=sQuery(id+"F8.wireOp",EDGE,"xjPRXnkF-zCrR-qSy3-F9DF-8FP80UqlAUpK");var subQ7=makeQuery(id+"F8.imprint","INTERSECT",VERTEX,{"disambiguationData":[OD(0.0)],"derivedFrom":[subQ6,subQ1]});Q21=makeQuery(id+"F8.imprint","IMPRINT",FACE,{"disambiguationData":[TD([[makeQuery(id+"F8.imprint","IMPRINT",EDGE,{"disambiguationData":[TD([[subQ7,1.0]])],"derivedFrom":subQ6}),-1.0]])]});}
            var Q22;
            {var subQ0=sQuery(id+"F8.wireOp",EDGE,"MK1JN8JD-Du2c-HQOb-NOSm-beTcnBK5B5G6");var subQ1=sQuery(id+"F8.wireOp",EDGE,"E22");var subQ2=makeQuery(id+"F8.imprint","INTERSECT",VERTEX,{"disambiguationData":[OD(1.0)],"derivedFrom":[subQ1,subQ0]});Q22=makeQuery(id+"F8.imprint","IMPRINT",FACE,{"disambiguationData":[TD([[makeQuery(id+"F8.imprint","IMPRINT",EDGE,{"disambiguationData":[TD([[subQ2,-1.0]])],"derivedFrom":subQ1}),-1.0]])]});}
            var Q23;
            {var subQ0=sQuery(id+"F8.wireOp",EDGE,"E30.0");var subQ1=sQuery(id+"F8.wireOp",EDGE,"CzXEVSpi-58KO-UlYB-svJQ-14zqcH1Ih517");var subQ2=makeQuery(id+"F8.imprint","INTERSECT",VERTEX,{"disambiguationData":[OD(1.0)],"derivedFrom":[subQ1,subQ0]});Q23=makeQuery(id+"F8.imprint","IMPRINT",FACE,{"disambiguationData":[TD([[makeQuery(id+"F8.imprint","IMPRINT",EDGE,{"disambiguationData":[TD([[subQ2,-1.0]])],"derivedFrom":subQ1}),-1.0]])]});}
            var Q24;
            {var subQ0=sQuery(id+"F8.wireOp",EDGE,"YXji5YEl-21Fw-Z43Q-9dM8-VWDDLNbWPz9D");var subQ1=sQuery(id+"F8.wireOp",EDGE,"CzXEVSpi-58KO-UlYB-svJQ-14zqcH1Ih517");var subQ2=makeQuery(id+"F8.imprint","INTERSECT",VERTEX,{"disambiguationData":[OD(0.0)],"derivedFrom":[subQ1,subQ0]});Q24=makeQuery(id+"F8.imprint","IMPRINT",FACE,{"disambiguationData":[TD([[makeQuery(id+"F8.imprint","IMPRINT",EDGE,{"disambiguationData":[TD([[subQ2,1.0]])],"derivedFrom":subQ1}),1.0]])]});}
            var Q25;
            {var subQ0=sQuery(id+"F8.wireOp",EDGE,"YXji5YEl-21Fw-Z43Q-9dM8-VWDDLNbWPz9D");var subQ1=sQuery(id+"F8.wireOp",EDGE,"CzXEVSpi-58KO-UlYB-svJQ-14zqcH1Ih517");var subQ2=makeQuery(id+"F8.imprint","INTERSECT",VERTEX,{"disambiguationData":[OD(0.0)],"derivedFrom":[subQ1,subQ0]});Q25=makeQuery(id+"F8.imprint","IMPRINT",FACE,{"disambiguationData":[TD([[makeQuery(id+"F8.imprint","IMPRINT",EDGE,{"disambiguationData":[TD([[subQ2,1.0]])],"derivedFrom":subQ1}),-1.0]])]});}
            var Q26;
            {var subQ0=sQuery(id+"F8.wireOp",EDGE,"E30.0");var subQ1=sQuery(id+"F8.wireOp",EDGE,"YXji5YEl-21Fw-Z43Q-9dM8-VWDDLNbWPz9D");var subQ2=makeQuery(id+"F8.imprint","INTERSECT",VERTEX,{"disambiguationData":[OD(0.0)],"derivedFrom":[subQ1,subQ0]});Q26=makeQuery(id+"F8.imprint","IMPRINT",FACE,{"disambiguationData":[TD([[makeQuery(id+"F8.imprint","IMPRINT",EDGE,{"disambiguationData":[TD([[subQ2,-1.0]])],"derivedFrom":subQ1}),1.0]])]});}
            var Q27;
            {var subQ0=sQuery(id+"F8.wireOp",EDGE,"E30.0");var subQ1=sQuery(id+"F8.wireOp",EDGE,"YXji5YEl-21Fw-Z43Q-9dM8-VWDDLNbWPz9D");var subQ2=makeQuery(id+"F8.imprint","INTERSECT",VERTEX,{"disambiguationData":[OD(1.0)],"derivedFrom":[subQ1,subQ0]});Q27=makeQuery(id+"F8.imprint","IMPRINT",FACE,{"disambiguationData":[TD([[makeQuery(id+"F8.imprint","IMPRINT",EDGE,{"disambiguationData":[TD([[subQ2,-1.0]])],"derivedFrom":subQ1}),-1.0]])]});}
            var Q28;
            {var subQ0=sQuery(id+"F8.wireOp",EDGE,"MK1JN8JD-Du2c-HQOb-NOSm-beTcnBK5B5G6");var subQ1=sQuery(id+"F8.wireOp",EDGE,"YXji5YEl-21Fw-Z43Q-9dM8-VWDDLNbWPz9D");var subQ2=makeQuery(id+"F8.imprint","INTERSECT",VERTEX,{"disambiguationData":[OD(0.0)],"derivedFrom":[subQ1,subQ0]});Q28=makeQuery(id+"F8.imprint","IMPRINT",FACE,{"disambiguationData":[TD([[makeQuery(id+"F8.imprint","IMPRINT",EDGE,{"disambiguationData":[TD([[subQ2,1.0]])],"derivedFrom":subQ1}),1.0]])]});}
            var Q29;
            {var subQ1=sQuery(id+"F8.wireOp",EDGE,"MK1JN8JD-Du2c-HQOb-NOSm-beTcnBK5B5G6");var subQ5=sQuery(id+"F8.wireOp",EDGE,"YXji5YEl-21Fw-Z43Q-9dM8-VWDDLNbWPz9D");var subQ6=makeQuery(id+"F8.imprint","INTERSECT",VERTEX,{"disambiguationData":[OD(0.0)],"derivedFrom":[subQ5,subQ1]});Q29=makeQuery(id+"F8.imprint","IMPRINT",FACE,{"disambiguationData":[TD([[makeQuery(id+"F8.imprint","IMPRINT",EDGE,{"disambiguationData":[TD([[subQ6,1.0]])],"derivedFrom":subQ5}),-1.0]])]});}
            var Q30;
            {var subQ0=sQuery(id+"F8.wireOp",EDGE,"kXx0Mqze-47q8-63xz-1Yix-Rh2NAVOSu0As");var subQ1=sQuery(id+"F8.wireOp",EDGE,"E22");var subQ2=makeQuery(id+"F8.imprint","INTERSECT",VERTEX,{"disambiguationData":[OD(0.0)],"derivedFrom":[subQ1,subQ0]});Q30=makeQuery(id+"F8.imprint","IMPRINT",FACE,{"disambiguationData":[TD([[makeQuery(id+"F8.imprint","IMPRINT",EDGE,{"disambiguationData":[TD([[subQ2,-1.0]])],"derivedFrom":subQ1}),-1.0]])]});}
            var Q31;
            {var subQ0=sQuery(id+"F8.wireOp",EDGE,"MK1JN8JD-Du2c-HQOb-NOSm-beTcnBK5B5G6");var subQ1=sQuery(id+"F8.wireOp",EDGE,"E22");var subQ2=makeQuery(id+"F8.imprint","INTERSECT",VERTEX,{"disambiguationData":[OD(0.0)],"derivedFrom":[subQ1,subQ0]});Q31=makeQuery(id+"F8.imprint","IMPRINT",FACE,{"disambiguationData":[TD([[makeQuery(id+"F8.imprint","IMPRINT",EDGE,{"disambiguationData":[TD([[subQ2,-1.0]])],"derivedFrom":subQ1}),-1.0]])]});}
            var Q32;
            {var subQ0=sQuery(id+"F8.wireOp",EDGE,"kXx0Mqze-47q8-63xz-1Yix-Rh2NAVOSu0As");var subQ1=sQuery(id+"F8.wireOp",EDGE,"MK1JN8JD-Du2c-HQOb-NOSm-beTcnBK5B5G6");var subQ2=makeQuery(id+"F8.imprint","INTERSECT",VERTEX,{"disambiguationData":[OD(0.0)],"derivedFrom":[subQ1,subQ0]});Q32=makeQuery(id+"F8.imprint","IMPRINT",FACE,{"disambiguationData":[TD([[makeQuery(id+"F8.imprint","IMPRINT",EDGE,{"disambiguationData":[TD([[subQ2,1.0]])],"derivedFrom":subQ1}),1.0]])]});}
            var Q33;
            {var subQ0=sQuery(id+"F8.wireOp",EDGE,"kXx0Mqze-47q8-63xz-1Yix-Rh2NAVOSu0As");var subQ1=sQuery(id+"F8.wireOp",EDGE,"MK1JN8JD-Du2c-HQOb-NOSm-beTcnBK5B5G6");var subQ2=makeQuery(id+"F8.imprint","INTERSECT",VERTEX,{"disambiguationData":[OD(0.0)],"derivedFrom":[subQ1,subQ0]});Q33=makeQuery(id+"F8.imprint","IMPRINT",FACE,{"disambiguationData":[TD([[makeQuery(id+"F8.imprint","IMPRINT",EDGE,{"disambiguationData":[TD([[subQ2,1.0]])],"derivedFrom":subQ1}),-1.0]])]});}
            var Q34;
            {var subQ1=sQuery(id+"F8.wireOp",EDGE,"E22");var subQ3=sQuery(id+"F8.wireOp",EDGE,"MK1JN8JD-Du2c-HQOb-NOSm-beTcnBK5B5G6");var subQ4=makeQuery(id+"F8.imprint","INTERSECT",VERTEX,{"disambiguationData":[OD(0.0)],"derivedFrom":[subQ1,subQ3]});Q34=makeQuery(id+"F8.imprint","IMPRINT",FACE,{"disambiguationData":[TD([[makeQuery(id+"F8.imprint","IMPRINT",EDGE,{"disambiguationData":[TD([[subQ4,-1.0]])],"derivedFrom":subQ3}),-1.0]])]});}
            var Q35;
            {var subQ0=sQuery(id+"F8.wireOp",EDGE,"kXx0Mqze-47q8-63xz-1Yix-Rh2NAVOSu0As");var subQ1=sQuery(id+"F8.wireOp",EDGE,"E22");var subQ2=makeQuery(id+"F8.imprint","INTERSECT",VERTEX,{"disambiguationData":[OD(1.0)],"derivedFrom":[subQ1,subQ0]});Q35=makeQuery(id+"F8.imprint","IMPRINT",FACE,{"disambiguationData":[TD([[makeQuery(id+"F8.imprint","IMPRINT",EDGE,{"disambiguationData":[TD([[subQ2,-1.0]])],"derivedFrom":subQ1}),-1.0]])]});}
            var Q36;
            {var subQ0=sQuery(id+"F8.wireOp",EDGE,"E29");var subQ1=sQuery(id+"F8.wireOp",EDGE,"E21");var subQ2=makeQuery(id+"F8.imprint","INTERSECT",VERTEX,{"derivedFrom":[subQ1,subQ0]});Q36=makeQuery(id+"F8.imprint","IMPRINT",FACE,{"disambiguationData":[TD([[makeQuery(id+"F8.imprint","IMPRINT",EDGE,{"disambiguationData":[TD([[subQ2,-1.0]])],"derivedFrom":subQ1}),1.0]])]});}
            var Q37;
            {var subQ0=sQuery(id+"F8.wireOp",EDGE,"E35.trimOffspring");Q37=makeQuery(id+"F8.imprint","IMPRINT",FACE,{"disambiguationData":[TD([[makeQuery(id+"F8.imprint","IMPRINT",EDGE,{"derivedFrom":subQ0}),-1.0]])]});}
            var Q38;
            {var subQ1=sQuery(id+"F8.wireOp",EDGE,"E22");var subQ7=sQuery(id+"F8.wireOp",EDGE,"E41.5");var subQ8=makeQuery(id+"F8.imprint","INTERSECT",VERTEX,{"derivedFrom":[subQ1,subQ7]});Q38=makeQuery(id+"F8.imprint","IMPRINT",FACE,{"disambiguationData":[TD([[makeQuery(id+"F8.imprint","IMPRINT",EDGE,{"disambiguationData":[TD([[subQ8,-1.0]])],"derivedFrom":subQ1}),-1.0]])]});}
            var Q39;
            {var subQ0=sQuery(id+"F8.wireOp",EDGE,"E30.0");var subQ9=sQuery(id+"F8.wireOp",EDGE,"E23");var subQ10=makeQuery(id+"F8.imprint","INTERSECT",VERTEX,{"derivedFrom":[subQ9,subQ0]});Q39=makeQuery(id+"F8.imprint","IMPRINT",FACE,{"disambiguationData":[TD([[makeQuery(id+"F8.imprint","IMPRINT",EDGE,{"disambiguationData":[TD([[subQ10,-1.0]])],"derivedFrom":subQ9}),-1.0]])]});}
            var Q40;
            {var subQ0=sQuery(id+"F8.wireOp",EDGE,"E24");var subQ1=sQuery(id+"F8.wireOp",EDGE,"E22");var subQ2=makeQuery(id+"F8.imprint","INTERSECT",VERTEX,{"derivedFrom":[subQ1,subQ0]});Q40=makeQuery(id+"F8.imprint","IMPRINT",FACE,{"disambiguationData":[TD([[makeQuery(id+"F8.imprint","IMPRINT",EDGE,{"disambiguationData":[TD([[subQ2,1.0]])],"derivedFrom":subQ1}),-1.0]])]});}
            var Q41;
            {var subQ0=sQuery(id+"F8.wireOp",EDGE,"E41.3");var subQ1=sQuery(id+"F8.wireOp",EDGE,"E24");var subQ2=makeQuery(id+"F8.imprint","INTERSECT",VERTEX,{"derivedFrom":[subQ1,subQ0]});Q41=makeQuery(id+"F8.imprint","IMPRINT",FACE,{"disambiguationData":[TD([[makeQuery(id+"F8.imprint","IMPRINT",EDGE,{"disambiguationData":[TD([[subQ2,-1.0]])],"derivedFrom":subQ1}),1.0]])]});}
            var Q42;
            {var subQ0=sQuery(id+"F0.wireOp",EDGE,"E1");var subQ1=sQuery(id+"F0.wireOp",EDGE,"E0");Q42=makeQuery(id+"F4.boolean.opBoolean","MERGE",FACE,{"derivedFrom":[makeQuery(id+"F1.opExtrude","CAP_FACE",FACE,{"disambiguationData":[OSD([subQ0,sQuery(id+"F0.wireOp",EDGE,"E2")])],"isStart":true})],"fromTools":[makeQuery(id+"F4.opExtrude","CAP_FACE",FACE,{"disambiguationData":[OSD([subQ1,subQ0,sQuery(id+"F3.wireOp",EDGE,"E17.right"),sQuery(id+"F3.wireOp",EDGE,"E18.1.3")])],"isStart":false}),makeQuery(id+"F4.opExtrude","CAP_FACE",FACE,{"disambiguationData":[OSD([subQ1,subQ0,sQuery(id+"F3.wireOp",EDGE,"E18.2.2"),sQuery(id+"F3.wireOp",EDGE,"E18.3.3")])],"isStart":false}),makeQuery(id+"F4.opExtrude","CAP_FACE",FACE,{"disambiguationData":[OSD([subQ1,subQ0,sQuery(id+"F3.wireOp",EDGE,"E18.4.2"),sQuery(id+"F3.wireOp",EDGE,"E18.5.3")])],"isStart":false})]});}
            extrude(context, id + "F9", {"entities" : qUnion([Q0, Q1, Q2, Q3, Q4, Q5, Q6, Q7, Q8, Q9, Q10, Q11, Q12, Q13, Q14, Q15, Q16, Q17, Q18, Q19, Q20, Q21, Q22, Q23, Q24, Q25, Q26, Q27, Q28, Q29, Q30, Q31, Q32, Q33, Q34, Q35, Q36, Q37, Q38, Q39, Q40, Q41]), "operationType" : NewBodyOperationType.ADD, "endBound" : BoundingType.UP_TO_SURFACE, "oppositeDirection" : true, "depth" : 25 * mm, "endBoundEntityFace" : qUnion([Q42]), "offsetDistance" : 25 * mm});
        }
        {
            var Q0;
            {var subQ0=sQuery(id+"F8.wireOp",EDGE,"E34.0");var subQ1=sQuery(id+"F8.wireOp",EDGE,"E29");var subQ2=makeQuery(id+"F8.imprint","INTERSECT",VERTEX,{"disambiguationData":[OD(0.0)],"derivedFrom":[subQ1,subQ0]});Q0=makeQuery(id+"F8.imprint","IMPRINT",FACE,{"disambiguationData":[TD([[makeQuery(id+"F8.imprint","IMPRINT",EDGE,{"disambiguationData":[TD([[subQ2,1.0]])],"derivedFrom":subQ1}),1.0]])]});}
            var Q1;
            {var subQ0=sQuery(id+"F8.wireOp",EDGE,"E34.0");var subQ1=sQuery(id+"F8.wireOp",EDGE,"E29");var subQ2=makeQuery(id+"F8.imprint","INTERSECT",VERTEX,{"disambiguationData":[OD(1.0)],"derivedFrom":[subQ1,subQ0]});Q1=makeQuery(id+"F8.imprint","IMPRINT",FACE,{"disambiguationData":[TD([[makeQuery(id+"F8.imprint","IMPRINT",EDGE,{"disambiguationData":[TD([[subQ2,-1.0]])],"derivedFrom":subQ1}),1.0]])]});}
            var Q2;
            {var subQ0=sQuery(id+"F0.wireOp",EDGE,"E2");var subQ1=sQuery(id+"F0.wireOp",EDGE,"E1");var subQ2=sQuery(id+"F0.wireOp",EDGE,"E0");Q2=makeQuery(id+"F9.boolean.opBoolean","MERGE",FACE,{"derivedFrom":[makeQuery(id+"F4.boolean.opBoolean","MERGE",FACE,{"derivedFrom":[makeQuery(id+"F1.opExtrude","CAP_FACE",FACE,{"disambiguationData":[OSD([subQ1,subQ0])],"isStart":true})],"fromTools":[makeQuery(id+"F4.opExtrude","CAP_FACE",FACE,{"disambiguationData":[OSD([subQ2,subQ1,sQuery(id+"F3.wireOp",EDGE,"E17.right"),sQuery(id+"F3.wireOp",EDGE,"E18.1.3")])],"isStart":false}),makeQuery(id+"F4.opExtrude","CAP_FACE",FACE,{"disambiguationData":[OSD([subQ2,subQ1,sQuery(id+"F3.wireOp",EDGE,"E18.2.2"),sQuery(id+"F3.wireOp",EDGE,"E18.3.3")])],"isStart":false}),makeQuery(id+"F4.opExtrude","CAP_FACE",FACE,{"disambiguationData":[OSD([subQ2,subQ1,sQuery(id+"F3.wireOp",EDGE,"E18.4.2"),sQuery(id+"F3.wireOp",EDGE,"E18.5.3")])],"isStart":false})]}),makeQuery(id+"F9.opExtrude","CAP_FACE",FACE,{"disambiguationData":[OSD([subQ0,sQuery(id+"F8.wireOp",EDGE,"E21"),sQuery(id+"F8.wireOp",EDGE,"E22"),sQuery(id+"F8.wireOp",EDGE,"E23"),sQuery(id+"F8.wireOp",EDGE,"E24"),sQuery(id+"F8.wireOp",EDGE,"ZrooK5EC-0a0A-ZKfd-yhxf-CoBbZ34mh2aH"),sQuery(id+"F8.wireOp",EDGE,"xjPRXnkF-zCrR-qSy3-F9DF-8FP80UqlAUpK"),sQuery(id+"F8.wireOp",EDGE,"CzXEVSpi-58KO-UlYB-svJQ-14zqcH1Ih517"),sQuery(id+"F8.wireOp",EDGE,"YXji5YEl-21Fw-Z43Q-9dM8-VWDDLNbWPz9D"),sQuery(id+"F8.wireOp",EDGE,"MK1JN8JD-Du2c-HQOb-NOSm-beTcnBK5B5G6"),sQuery(id+"F8.wireOp",EDGE,"kXx0Mqze-47q8-63xz-1Yix-Rh2NAVOSu0As"),sQuery(id+"F8.wireOp",EDGE,"E25.0"),sQuery(id+"F8.wireOp",EDGE,"E26.0"),sQuery(id+"F8.wireOp",EDGE,"E27"),sQuery(id+"F8.wireOp",EDGE,"E29"),sQuery(id+"F8.wireOp",EDGE,"E30.0"),sQuery(id+"F8.wireOp",EDGE,"E31.MirrorCS"),sQuery(id+"F8.wireOp",EDGE,"E32.MirrorCS"),sQuery(id+"F8.wireOp",EDGE,"E33.MirrorCS")])],"isStart":false})]});}
            extrude(context, id + "F10", {"entities" : qUnion([Q0, Q1]), "operationType" : NewBodyOperationType.REMOVE, "endBound" : BoundingType.UP_TO_SURFACE, "oppositeDirection" : true, "depth" : 25 * mm, "endBoundEntityFace" : qUnion([Q2]), "offsetDistance" : 25 * mm});
        }
    });
